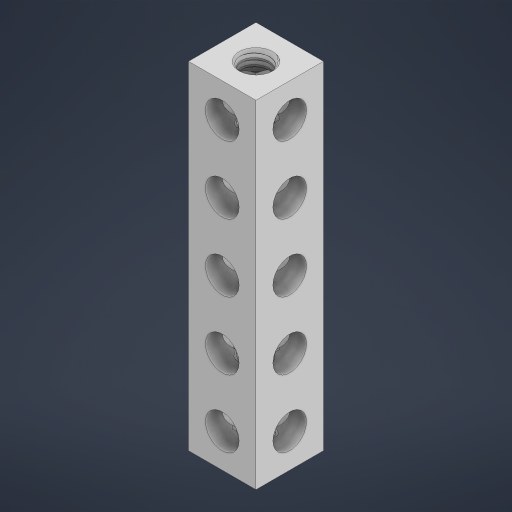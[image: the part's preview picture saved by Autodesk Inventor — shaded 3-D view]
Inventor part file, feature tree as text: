
AUTODESK INVENTOR PART (.ipt)
format: ipt  version: 2023 (Build 270158000, 158)  size: 1,315,328 bytes
history: native  units: in
note: dims shown in document units (in); Inventor stores cm internally (conversion verified against a paired STEP export)
features: mirror x1
ambient origin geometry x8: Origin, YZ Plane, XZ Plane, XY Plane, X Axis, Y Axis, Z Axis, Center Point
bodies: Solid1 (feature_tree)
feature tree (1):
  mirror  "Mirror3"
